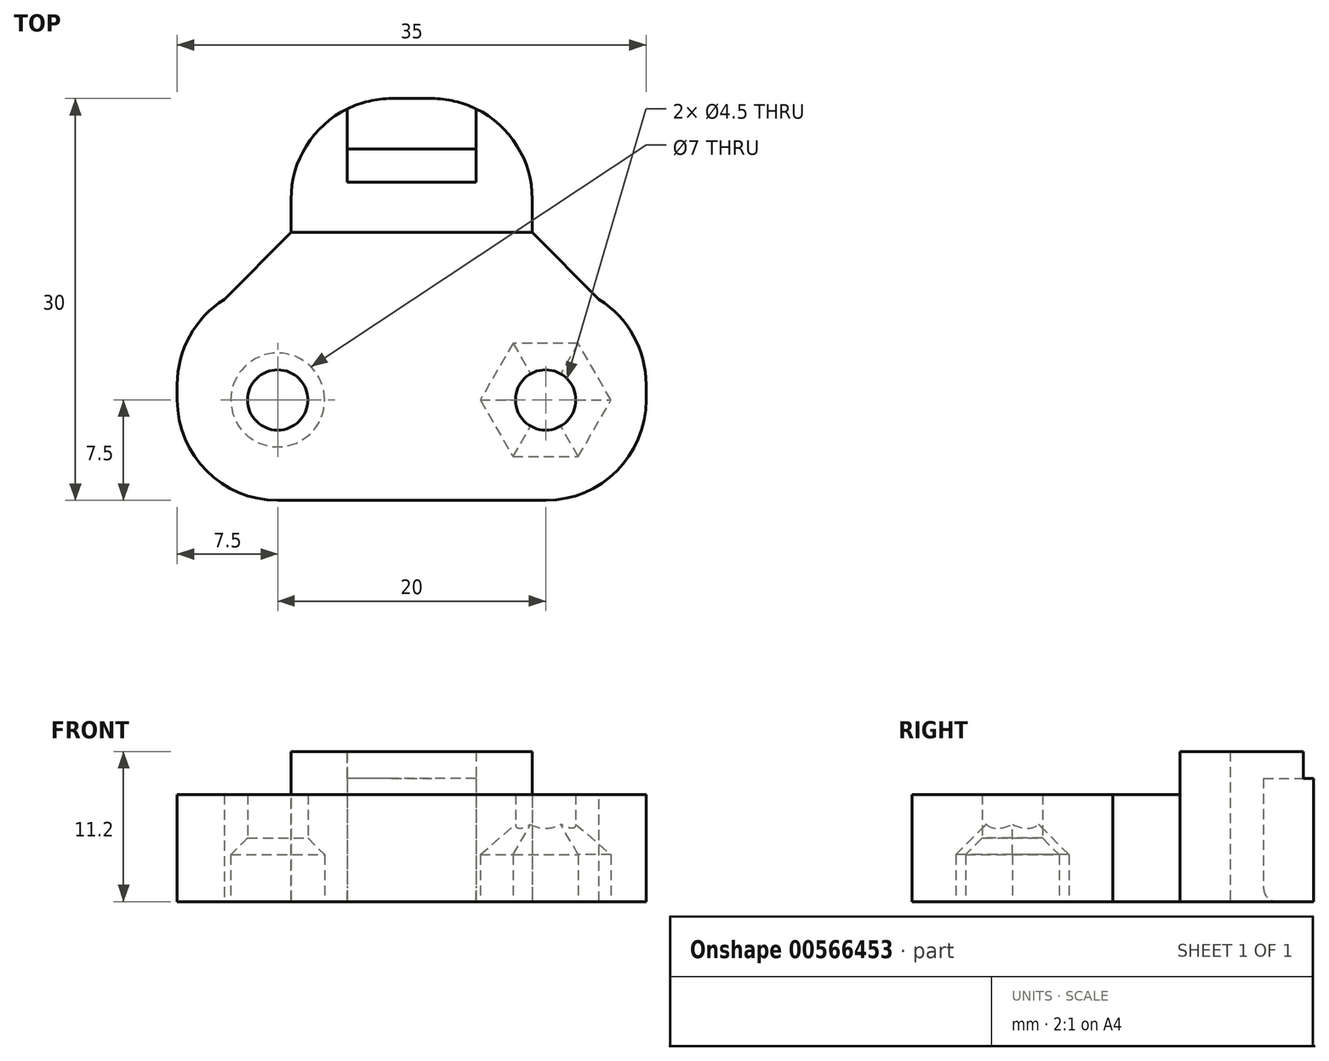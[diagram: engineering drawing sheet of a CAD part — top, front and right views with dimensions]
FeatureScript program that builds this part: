
annotation { "Feature Type Name" : "Feature", "Feature Type Description" : "" }
export const myFeature = defineFeature(function(context is Context, id is Id, definition is map)
    precondition{}
    {
        {
            var Q0;
            Q0=qCreatedBy(makeId("Top.planeOp"),FACE);
            var sketch = newSketch(context, id + "F0", { "sketchPlane" : qUnion([Q0])});
            skLineSegment(sketch, "E0.bottom", {"start": v(17.5, -7.5) * mm, "end": v(-17.5, -7.5) * mm});
            skLineSegment(sketch, "E0.top", {"start": v(17.5, 7.5) * mm, "end": v(9, 7.5) * mm});
            skLineSegment(sketch, "E0.left", {"start": v(17.5, -7.5) * mm, "end": v(17.5, 7.5) * mm});
            skLineSegment(sketch, "E0.right", {"start": v(-17.5, -7.5) * mm, "end": v(-17.5, 7.5) * mm});
            skPoint(sketch, "E0.middle", {"position": v(0, 0) * mm});
            skCircle(sketch, "E1", {"center": v(-10, 0) * mm, "radius": 2.25 * mm});
            skCircle(sketch, "E2.MirrorC", {"center": v(10, 0) * mm, "radius": 2.25 * mm});
            skLineSegment(sketch, "E3", {"start": v(-9, 7.5) * mm, "end": v(-9, 22.5) * mm});
            skLineSegment(sketch, "E4", {"start": v(-9, 22.5) * mm, "end": v(0, 22.5) * mm});
            skLineSegment(sketch, "E5.MirrorCS", {"start": v(9, 22.5) * mm, "end": v(0, 22.5) * mm});
            skLineSegment(sketch, "E6.MirrorCS", {"start": v(9, 7.5) * mm, "end": v(9, 22.5) * mm});
            skLineSegment(sketch, "E7.bottom", {"start": v(4.8, 16.25) * mm, "end": v(-4.8, 16.25) * mm});
            skLineSegment(sketch, "E7.top", {"start": v(4.8, 18.75) * mm, "end": v(-4.8, 18.75) * mm});
            skLineSegment(sketch, "E7.left", {"start": v(4.8, 16.25) * mm, "end": v(4.8, 18.75) * mm});
            skLineSegment(sketch, "E7.right", {"start": v(-4.8, 16.25) * mm, "end": v(-4.8, 18.75) * mm});
            skPoint(sketch, "E7.middle", {"position": v(0, 17.5) * mm});
            skLineSegment(sketch, "E8.trimOffspring", {"start": v(-9, 7.5) * mm, "end": v(-17.5, 7.5) * mm});
            skSolve(sketch);
        }
        {
            var Q0;
            Q0=qSketchRegion(id+"F0",true);
            extrude(context, id + "F1", {"entities" : qUnion([Q0]), "depth" : 8 * mm, "offsetDistance" : 25 * mm});
        }
        {
            var Q0;
            Q0=makeQuery(id+"F1.opExtrude","SWEPT_EDGE",EDGE,{"disambiguationData":[OSD([sQuery(id+"F0.wireOp",EDGE,"E3"),sQuery(id+"F0.wireOp",EDGE,"E8.trimOffspring")])]});
            var Q1;
            Q1=makeQuery(id+"F1.opExtrude","SWEPT_EDGE",EDGE,{"disambiguationData":[OSD([sQuery(id+"F0.wireOp",EDGE,"E0.top"),sQuery(id+"F0.wireOp",EDGE,"E6.MirrorCS")])]});
            chamfer(context, id + "F2", {"entities" : qUnion([Q0, Q1]), "width" : 5 * mm, "tangentPropagation" : true});
        }
        {
            var Q0;
            Q0=makeQuery(id+"F1.opExtrude","CAP_FACE",FACE,{"disambiguationData":[OSD([sQuery(id+"F0.wireOp",EDGE,"E0.bottom"),sQuery(id+"F0.wireOp",EDGE,"E0.top"),sQuery(id+"F0.wireOp",EDGE,"E0.left"),sQuery(id+"F0.wireOp",EDGE,"E0.right"),sQuery(id+"F0.wireOp",EDGE,"E1"),sQuery(id+"F0.wireOp",EDGE,"E2.MirrorC"),sQuery(id+"F0.wireOp",EDGE,"E3"),sQuery(id+"F0.wireOp",EDGE,"E4"),sQuery(id+"F0.wireOp",EDGE,"E5.MirrorCS"),sQuery(id+"F0.wireOp",EDGE,"E6.MirrorCS"),sQuery(id+"F0.wireOp",EDGE,"E7.bottom"),sQuery(id+"F0.wireOp",EDGE,"E7.top"),sQuery(id+"F0.wireOp",EDGE,"E7.left"),sQuery(id+"F0.wireOp",EDGE,"E7.right"),sQuery(id+"F0.wireOp",EDGE,"E8.trimOffspring")])],"isStart":false});
            var sketch = newSketch(context, id + "F3", { "sketchPlane" : qUnion([Q0])});
            skLineSegment(sketch, "E9.bottom", {"start": v(4.8, 16.25) * mm, "end": v(-4.8, 16.25) * mm});
            skLineSegment(sketch, "E9.top", {"start": v(4.8, 18.75) * mm, "end": v(-4.8, 18.75) * mm});
            skLineSegment(sketch, "E9.left", {"start": v(4.8, 16.25) * mm, "end": v(4.8, 18.75) * mm});
            skLineSegment(sketch, "E9.right", {"start": v(-4.8, 16.25) * mm, "end": v(-4.8, 18.75) * mm});
            skPoint(sketch, "E9.middle", {"position": v(0, 17.5) * mm});
            skLineSegment(sketch, "E10.bottom", {"start": v(9, 12.5) * mm, "end": v(-9, 12.5) * mm});
            skLineSegment(sketch, "E10.top", {"start": v(9, 22.5) * mm, "end": v(-9, 22.5) * mm});
            skLineSegment(sketch, "E10.left", {"start": v(9, 12.5) * mm, "end": v(9, 22.5) * mm});
            skLineSegment(sketch, "E10.right", {"start": v(-9, 12.5) * mm, "end": v(-9, 22.5) * mm});
            skSolve(sketch);
        }
        {
            var Q0;
            Q0=qSketchRegion(id+"F3",true);
            extrude(context, id + "F4", {"entities" : qUnion([Q0]), "operationType" : NewBodyOperationType.ADD, "depth" : 3.2 * mm, "offsetDistance" : 25 * mm});
        }
        {
            var Q0;
            Q0=makeQuery(id+"F1.opExtrude","SWEPT_EDGE",EDGE,{"disambiguationData":[OSD([sQuery(id+"F0.wireOp",EDGE,"E5.MirrorCS"),sQuery(id+"F0.wireOp",EDGE,"E6.MirrorCS")])]});
            var Q1;
            Q1=makeQuery(id+"F1.opExtrude","SWEPT_EDGE",EDGE,{"disambiguationData":[OSD([sQuery(id+"F0.wireOp",EDGE,"E3"),sQuery(id+"F0.wireOp",EDGE,"E4")])]});
            var Q2;
            Q2=makeQuery(id+"F1.opExtrude","SWEPT_EDGE",EDGE,{"disambiguationData":[OSD([sQuery(id+"F0.wireOp",EDGE,"E0.right"),sQuery(id+"F0.wireOp",EDGE,"E8.trimOffspring")])]});
            var Q3;
            Q3=makeQuery(id+"F1.opExtrude","SWEPT_EDGE",EDGE,{"disambiguationData":[OSD([sQuery(id+"F0.wireOp",EDGE,"E0.top"),sQuery(id+"F0.wireOp",EDGE,"E0.left")])]});
            var Q4;
            Q4=makeQuery(id+"F1.opExtrude","SWEPT_EDGE",EDGE,{"disambiguationData":[OSD([sQuery(id+"F0.wireOp",EDGE,"E0.bottom"),sQuery(id+"F0.wireOp",EDGE,"E0.left")])]});
            var Q5;
            Q5=makeQuery(id+"F1.opExtrude","SWEPT_EDGE",EDGE,{"disambiguationData":[OSD([sQuery(id+"F0.wireOp",EDGE,"E0.bottom"),sQuery(id+"F0.wireOp",EDGE,"E0.right")])]});
            fillet(context, id + "F5", {"entities" : qUnion([Q0, Q1, Q2, Q3, Q4, Q5]), "radius" : 7.5 * mm, "tangentPropagation" : true, "allowEdgeOverflow" : false});
        }
        {
            var Q0;
            Q0=makeQuery(id+"F1.opExtrude","CAP_FACE",FACE,{"disambiguationData":[OSD([sQuery(id+"F0.wireOp",EDGE,"E0.bottom"),sQuery(id+"F0.wireOp",EDGE,"E0.top"),sQuery(id+"F0.wireOp",EDGE,"E0.left"),sQuery(id+"F0.wireOp",EDGE,"E0.right"),sQuery(id+"F0.wireOp",EDGE,"E1"),sQuery(id+"F0.wireOp",EDGE,"E2.MirrorC"),sQuery(id+"F0.wireOp",EDGE,"E3"),sQuery(id+"F0.wireOp",EDGE,"E4"),sQuery(id+"F0.wireOp",EDGE,"E5.MirrorCS"),sQuery(id+"F0.wireOp",EDGE,"E6.MirrorCS"),sQuery(id+"F0.wireOp",EDGE,"E7.bottom"),sQuery(id+"F0.wireOp",EDGE,"E7.top"),sQuery(id+"F0.wireOp",EDGE,"E7.left"),sQuery(id+"F0.wireOp",EDGE,"E7.right"),sQuery(id+"F0.wireOp",EDGE,"E8.trimOffspring")])],"isStart":true});
            var sketch = newSketch(context, id + "F6", { "sketchPlane" : qUnion([Q0])});
            skCircle(sketch, "E11", {"center": v(-10, 0) * mm, "radius": 3.5 * mm});
            skCircle(sketch, "E12.cCircle", {"center": v(10, 0) * mm, "radius": 4.22 * mm, "construction": true});
            skLineSegment(sketch, "E12.0", {"start": v(7.56, 4.22) * mm, "end": v(12.44, 4.22) * mm});
            skLineSegment(sketch, "E12.1", {"start": v(12.44, 4.23) * mm, "end": v(14.88, 0) * mm});
            skLineSegment(sketch, "E12.2", {"start": v(14.88, 0) * mm, "end": v(12.44, -4.22) * mm});
            skLineSegment(sketch, "E12.3", {"start": v(12.44, -4.22) * mm, "end": v(7.56, -4.22) * mm});
            skLineSegment(sketch, "E12.4", {"start": v(7.56, -4.23) * mm, "end": v(5.12, 0) * mm});
            skLineSegment(sketch, "E12.5", {"start": v(5.12, 0) * mm, "end": v(7.56, 4.22) * mm});
            skPoint(sketch, "E12.0.midPoint", {"position": v(10, 4.22) * mm});
            skSolve(sketch);
        }
        {
            var Q0;
            Q0=qSketchRegion(id+"F6",true);
            extrude(context, id + "F7", {"entities" : qUnion([Q0]), "operationType" : NewBodyOperationType.REMOVE, "oppositeDirection" : true, "depth" : 6 * mm, "offsetDistance" : 25 * mm});
        }
        {
            var Q0;
            Q0=makeQuery(id+"F7.boolean.opBoolean","COPY",EDGE,{"derivedFrom":makeQuery(id+"F7.opExtrude","CAP_EDGE",EDGE,{"disambiguationData":[OSD([sQuery(id+"F6.wireOp",EDGE,"E11")])],"isStart":false})});
            var Q1;
            Q1=makeQuery(id+"F7.boolean.opBoolean","COPY",EDGE,{"derivedFrom":makeQuery(id+"F7.opExtrude","CAP_EDGE",EDGE,{"disambiguationData":[OSD([sQuery(id+"F6.wireOp",EDGE,"E12.5")])],"isStart":false})});
            var Q2;
            Q2=makeQuery(id+"F7.boolean.opBoolean","COPY",EDGE,{"derivedFrom":makeQuery(id+"F7.opExtrude","CAP_EDGE",EDGE,{"disambiguationData":[OSD([sQuery(id+"F6.wireOp",EDGE,"E12.4")])],"isStart":false})});
            var Q3;
            Q3=makeQuery(id+"F7.boolean.opBoolean","COPY",EDGE,{"derivedFrom":makeQuery(id+"F7.opExtrude","CAP_EDGE",EDGE,{"disambiguationData":[OSD([sQuery(id+"F6.wireOp",EDGE,"E12.3")])],"isStart":false})});
            var Q4;
            Q4=makeQuery(id+"F7.boolean.opBoolean","COPY",EDGE,{"derivedFrom":makeQuery(id+"F7.opExtrude","CAP_EDGE",EDGE,{"disambiguationData":[OSD([sQuery(id+"F6.wireOp",EDGE,"E12.2")])],"isStart":false})});
            var Q5;
            Q5=makeQuery(id+"F7.boolean.opBoolean","COPY",EDGE,{"derivedFrom":makeQuery(id+"F7.opExtrude","CAP_EDGE",EDGE,{"disambiguationData":[OSD([sQuery(id+"F6.wireOp",EDGE,"E12.1")])],"isStart":false})});
            var Q6;
            Q6=makeQuery(id+"F7.boolean.opBoolean","COPY",EDGE,{"derivedFrom":makeQuery(id+"F7.opExtrude","CAP_EDGE",EDGE,{"disambiguationData":[OSD([sQuery(id+"F6.wireOp",EDGE,"E12.0")])],"isStart":false})});
            chamfer(context, id + "F8", {"entities" : qUnion([Q0, Q1, Q2, Q3, Q4, Q5, Q6]), "width" : 2.5 * mm, "tangentPropagation" : true});
        }
        {
            var Q0;
            Q0=makeQuery(id+"F4.opExtrude","CAP_FACE",FACE,{"disambiguationData":[OSD([sQuery(id+"F3.wireOp",EDGE,"E9.bottom"),sQuery(id+"F3.wireOp",EDGE,"E9.top"),sQuery(id+"F3.wireOp",EDGE,"E9.left"),sQuery(id+"F3.wireOp",EDGE,"E9.right"),sQuery(id+"F3.wireOp",EDGE,"E10.bottom"),sQuery(id+"F3.wireOp",EDGE,"E10.top"),sQuery(id+"F3.wireOp",EDGE,"E10.left"),sQuery(id+"F3.wireOp",EDGE,"E10.right")])],"isStart":false});
            var sketch = newSketch(context, id + "F9", { "sketchPlane" : qUnion([Q0])});
            skLineSegment(sketch, "E13.bottom", {"start": v(-4.8, 18.75) * mm, "end": v(4.8, 18.75) * mm});
            skLineSegment(sketch, "E13.top", {"start": v(-4.8, 22.5) * mm, "end": v(4.8, 22.5) * mm});
            skLineSegment(sketch, "E13.left", {"start": v(-4.8, 18.75) * mm, "end": v(-4.8, 22.5) * mm});
            skLineSegment(sketch, "E13.right", {"start": v(4.8, 18.75) * mm, "end": v(4.8, 22.5) * mm});
            skSolve(sketch);
        }
        {
            var Q0;
            Q0=qSketchRegion(id+"F9",true);
            extrude(context, id + "F10", {"entities" : qUnion([Q0]), "operationType" : NewBodyOperationType.REMOVE, "oppositeDirection" : true, "depth" : 2 * mm, "offsetDistance" : 25 * mm});
        }
        {
            var Q0;
            Q0=makeQuery(id+"F1.opExtrude","CAP_EDGE",EDGE,{"disambiguationData":[OSD([sQuery(id+"F0.wireOp",EDGE,"E7.top")])],"isStart":true});
            var Q1;
            Q1=makeQuery(id+"F10.boolean.opBoolean","COPY",EDGE,{"derivedFrom":makeQuery(id+"F10.opExtrude","CAP_EDGE",EDGE,{"disambiguationData":[OSD([sQuery(id+"F9.wireOp",EDGE,"E13.bottom")])],"isStart":false})});
            fillet(context, id + "F11", {"entities" : qUnion([Q0, Q1]), "radius" : 1 * mm, "tangentPropagation" : true, "allowEdgeOverflow" : false});
        }
    });
